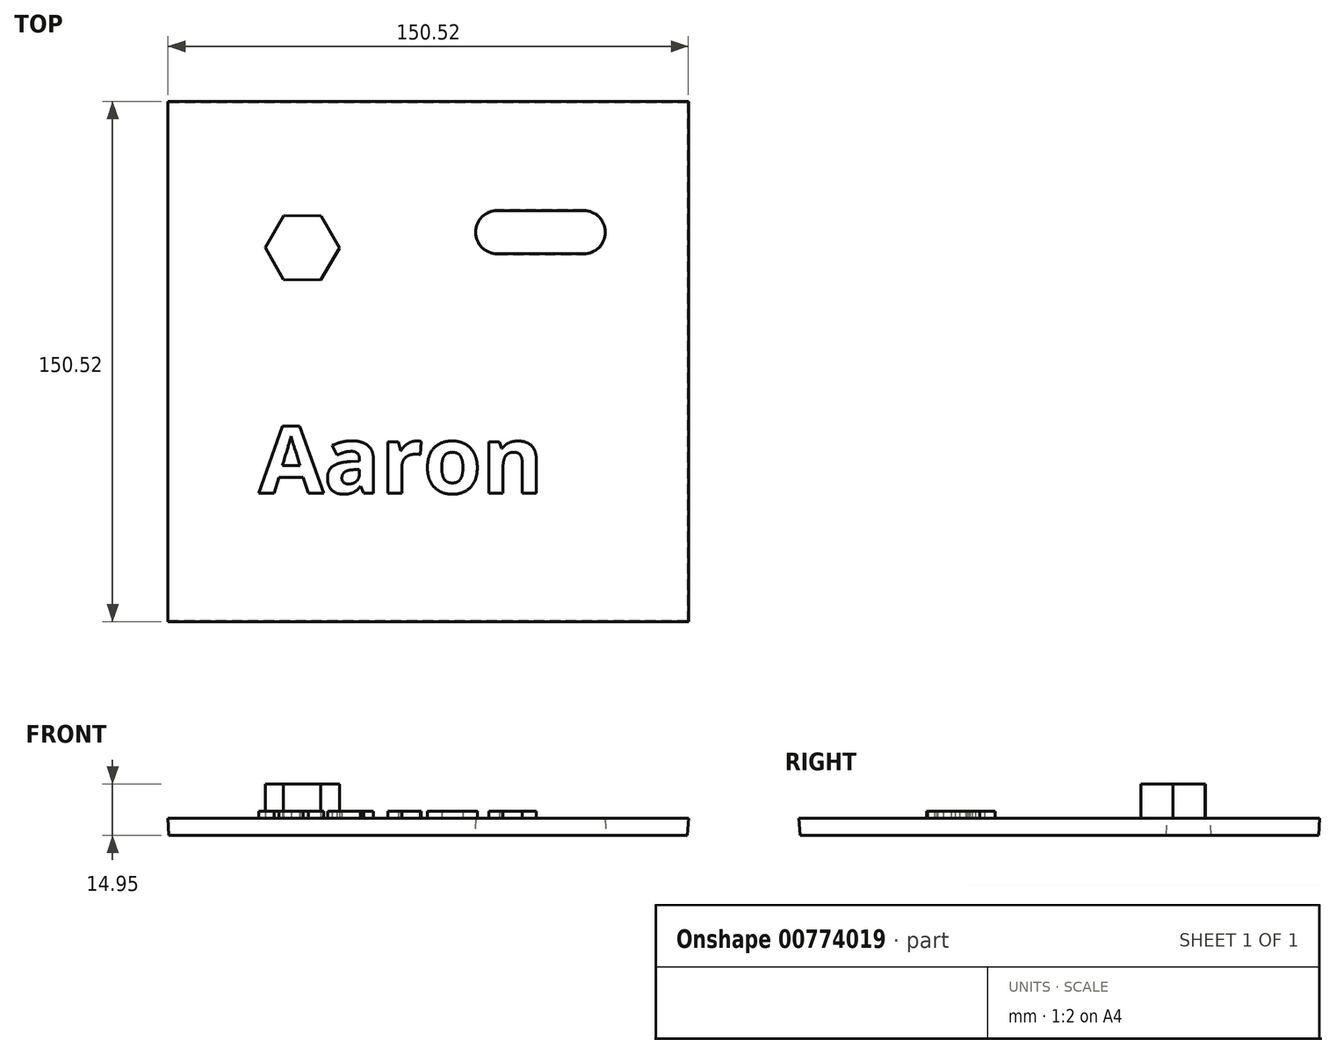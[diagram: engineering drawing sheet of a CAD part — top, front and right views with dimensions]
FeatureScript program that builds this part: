
annotation { "Feature Type Name" : "Feature", "Feature Type Description" : "" }
export const myFeature = defineFeature(function(context is Context, id is Id, definition is map)
    precondition{}
    {
        {
            var Q0;
            Q0=qCreatedBy(makeId("Top.planeOp"),FACE);
            var sketch = newSketch(context, id + "F0", { "sketchPlane" : qUnion([Q0])});
            skLineSegment(sketch, "E0.bottom", {"start": v(-75, -75) * mm, "end": v(75, -75) * mm});
            skLineSegment(sketch, "E0.top", {"start": v(-75, 75) * mm, "end": v(75, 75) * mm});
            skLineSegment(sketch, "E0.left", {"start": v(-75, -75) * mm, "end": v(-75, 75) * mm});
            skLineSegment(sketch, "E0.right", {"start": v(75, -75) * mm, "end": v(75, 75) * mm});
            skLineSegment(sketch, "E1", {"start": v(0, 75) * mm, "end": v(0, -75) * mm});
            skLineSegment(sketch, "E2", {"start": v(0, -75) * mm, "end": v(-75, 0) * mm, "construction": true});
            skLineSegment(sketch, "E3", {"start": v(-75, 0) * mm, "end": v(75, 0) * mm});
            skArc(sketch, "E4.0.startCap", {"start": v(1.77, -73.23) * mm, "mid": v(1.77, -76.77) * mm, "end": v(-1.77, -76.77) * mm, "construction": true});
            skArc(sketch, "E4.0.endCap", {"start": v(-76.77, -1.77) * mm, "mid": v(-76.77, 1.77) * mm, "end": v(-73.23, 1.77) * mm, "construction": true});
            skLineSegment(sketch, "E4.0.left", {"start": v(-1.77, -76.77) * mm, "end": v(-76.77, -1.77) * mm, "construction": true});
            skLineSegment(sketch, "E4.0.right", {"start": v(1.77, -73.23) * mm, "end": v(-73.23, 1.77) * mm, "construction": true});
            skArc(sketch, "E5.0.startCap", {"start": v(4.5, -70.5) * mm, "mid": v(4.5, -79.5) * mm, "end": v(-4.5, -79.5) * mm, "construction": true});
            skArc(sketch, "E5.0.endCap", {"start": v(-79.5, -4.5) * mm, "mid": v(-79.5, 4.5) * mm, "end": v(-70.5, 4.5) * mm, "construction": true});
            skLineSegment(sketch, "E5.0.left", {"start": v(-4.5, -79.5) * mm, "end": v(-79.5, -4.5) * mm, "construction": true});
            skLineSegment(sketch, "E5.0.right", {"start": v(4.5, -70.5) * mm, "end": v(-70.5, 4.5) * mm, "construction": true});
            skLineSegment(sketch, "E6", {"start": v(19.98, 37.46) * mm, "end": v(44.98, 37.46) * mm});
            skArc(sketch, "E7.0.startCap", {"start": v(19.98, 30.96) * mm, "mid": v(13.48, 37.46) * mm, "end": v(19.98, 43.96) * mm});
            skArc(sketch, "E7.0.endCap", {"start": v(44.98, 43.96) * mm, "mid": v(51.48, 37.46) * mm, "end": v(44.98, 30.96) * mm});
            skLineSegment(sketch, "E7.0.left", {"start": v(19.98, 43.96) * mm, "end": v(44.98, 43.96) * mm});
            skLineSegment(sketch, "E7.0.right", {"start": v(19.98, 30.96) * mm, "end": v(44.98, 30.96) * mm});
            skSolve(sketch);
        }
        {
            var Q0;
            Q0 = qSketchRegion(id + "F0", true);
            extrude(context, id + "F1", {"entities" : qUnion([Q0]), "depth" : 5 * mm, "offsetDistance" : 25 * mm, "hasDraft" : true, "draftAngle" : 3 * degree});
        }
        {
            var Q0;
            Q0=makeQuery(id+"F1.opExtrude","CAP_FACE",FACE,{"disambiguationData":[OSD([sQuery(id+"F0.wireOp",EDGE,"E0.bottom"),sQuery(id+"F0.wireOp",EDGE,"E0.top"),sQuery(id+"F0.wireOp",EDGE,"E0.left"),sQuery(id+"F0.wireOp",EDGE,"E0.right"),sQuery(id+"F0.wireOp",EDGE,"E7.0.startCap"),sQuery(id+"F0.wireOp",EDGE,"E7.0.endCap"),sQuery(id+"F0.wireOp",EDGE,"E7.0.left"),sQuery(id+"F0.wireOp",EDGE,"E7.0.right")])],"isStart":false});
            var sketch = newSketch(context, id + "F2", { "sketchPlane" : qUnion([Q0])});
            skText(sketch, "E8", { "text": "Aaron", "fontName": "OpenSans-Bold.ttf"});
            const initialGuessF2  = {"E8": [-0.04906, -0.03813, 1, 0, 0.01961]};
            skSetInitialGuess(sketch, initialGuessF2);
            skSolve(sketch);
        }
        {
            var Q0;
            Q0 = qSketchRegion(id + "F2", true);
            extrude(context, id + "F3", {"entities" : qUnion([Q0]), "operationType" : NewBodyOperationType.ADD, "depth" : 2 * mm, "offsetDistance" : 25 * mm});
        }
        {
            var Q0;
            {var subQ0=sQuery(id+"F0.wireOp",EDGE,"E7.0.left");var subQ1=sQuery(id+"F0.wireOp",EDGE,"E7.0.right");var subQ2=sQuery(id+"F0.wireOp",EDGE,"E7.0.endCap");var subQ3=sQuery(id+"F0.wireOp",EDGE,"E7.0.startCap");var subQ4=sQuery(id+"F0.wireOp",EDGE,"E0.bottom");var subQ5=sQuery(id+"F0.wireOp",EDGE,"E0.right");var subQ6=sQuery(id+"F0.wireOp",EDGE,"E0.top");var subQ7=sQuery(id+"F0.wireOp",EDGE,"E0.left");Q0=makeQuery(id+"F3.boolean.opBoolean","SPLIT",FACE,{"disambiguationData":[TD([makeQuery(id+"F1.opExtrude","SWEPT_FACE",FACE,{"disambiguationData":[OSD([subQ4])]})])],"derivedFrom":makeQuery(id+"F1.opExtrude","CAP_FACE",FACE,{"disambiguationData":[OSD([subQ4,subQ6,subQ7,subQ5,subQ3,subQ2,subQ0,subQ1])],"isStart":false})});}
            var sketch = newSketch(context, id + "F4", { "sketchPlane" : qUnion([Q0])});
            skCircle(sketch, "E9.cCircle", {"center": v(-36.43, 32.95) * mm, "radius": 10.73 * mm, "construction": true});
            skLineSegment(sketch, "E9.0", {"start": v(-25.7, 32.86) * mm, "end": v(-31.14, 23.61) * mm});
            skLineSegment(sketch, "E9.1", {"start": v(-31.14, 23.61) * mm, "end": v(-41.87, 23.7) * mm});
            skLineSegment(sketch, "E9.2", {"start": v(-41.87, 23.7) * mm, "end": v(-47.16, 33.03) * mm});
            skLineSegment(sketch, "E9.3", {"start": v(-47.16, 33.03) * mm, "end": v(-41.72, 42.28) * mm});
            skLineSegment(sketch, "E9.4", {"start": v(-41.72, 42.28) * mm, "end": v(-30.99, 42.2) * mm});
            skLineSegment(sketch, "E9.5", {"start": v(-30.99, 42.2) * mm, "end": v(-25.7, 32.86) * mm});
            skSolve(sketch);
        }
        {
            var Q0;
            Q0=makeQuery(id+"F4.imprint","IMPRINT",FACE,{"disambiguationData":[TD([[makeQuery(id+"F4.imprint","IMPRINT",EDGE,{"derivedFrom":sQuery(id+"F4.wireOp",EDGE,"E9.0")}),-1.0]])]});
            extrude(context, id + "F5", {"entities" : qUnion([Q0]), "operationType" : NewBodyOperationType.ADD, "depth" : 9.95 * mm, "offsetDistance" : 25 * mm});
        }
    });
